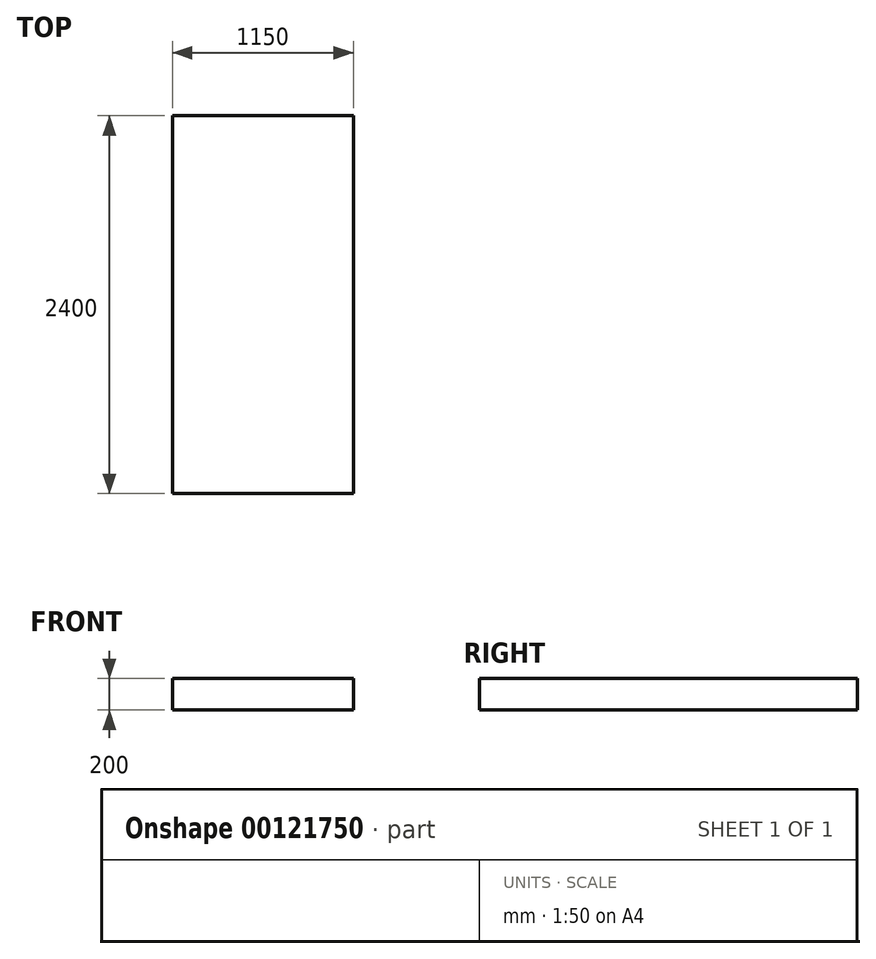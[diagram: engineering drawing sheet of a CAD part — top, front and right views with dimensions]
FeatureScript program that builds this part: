
annotation { "Feature Type Name" : "Feature", "Feature Type Description" : "" }
export const myFeature = defineFeature(function(context is Context, id is Id, definition is map)
    precondition{}
    {
        {
            var Q0;
            Q0=qCreatedBy(makeId("Top.planeOp"),FACE);
            var sketch = newSketch(context, id + "F0", { "sketchPlane" : qUnion([Q0])});
            skLineSegment(sketch, "E0.bottom", {"start": v(575, -1200) * mm, "end": v(-575, -1200) * mm});
            skLineSegment(sketch, "E0.top", {"start": v(575, 1200) * mm, "end": v(-575, 1200) * mm});
            skLineSegment(sketch, "E0.left", {"start": v(575, -1200) * mm, "end": v(575, 1200) * mm});
            skLineSegment(sketch, "E0.right", {"start": v(-575, -1200) * mm, "end": v(-575, 1200) * mm});
            skPoint(sketch, "E0.middle", {"position": v(0, 0) * mm});
            skSolve(sketch);
        }
        {
            var Q0;
            Q0 = qSketchRegion(id + "F0", true);
            extrude(context, id + "F1", {"entities" : qUnion([Q0]), "depth" : 200 * mm});
        }
    });
